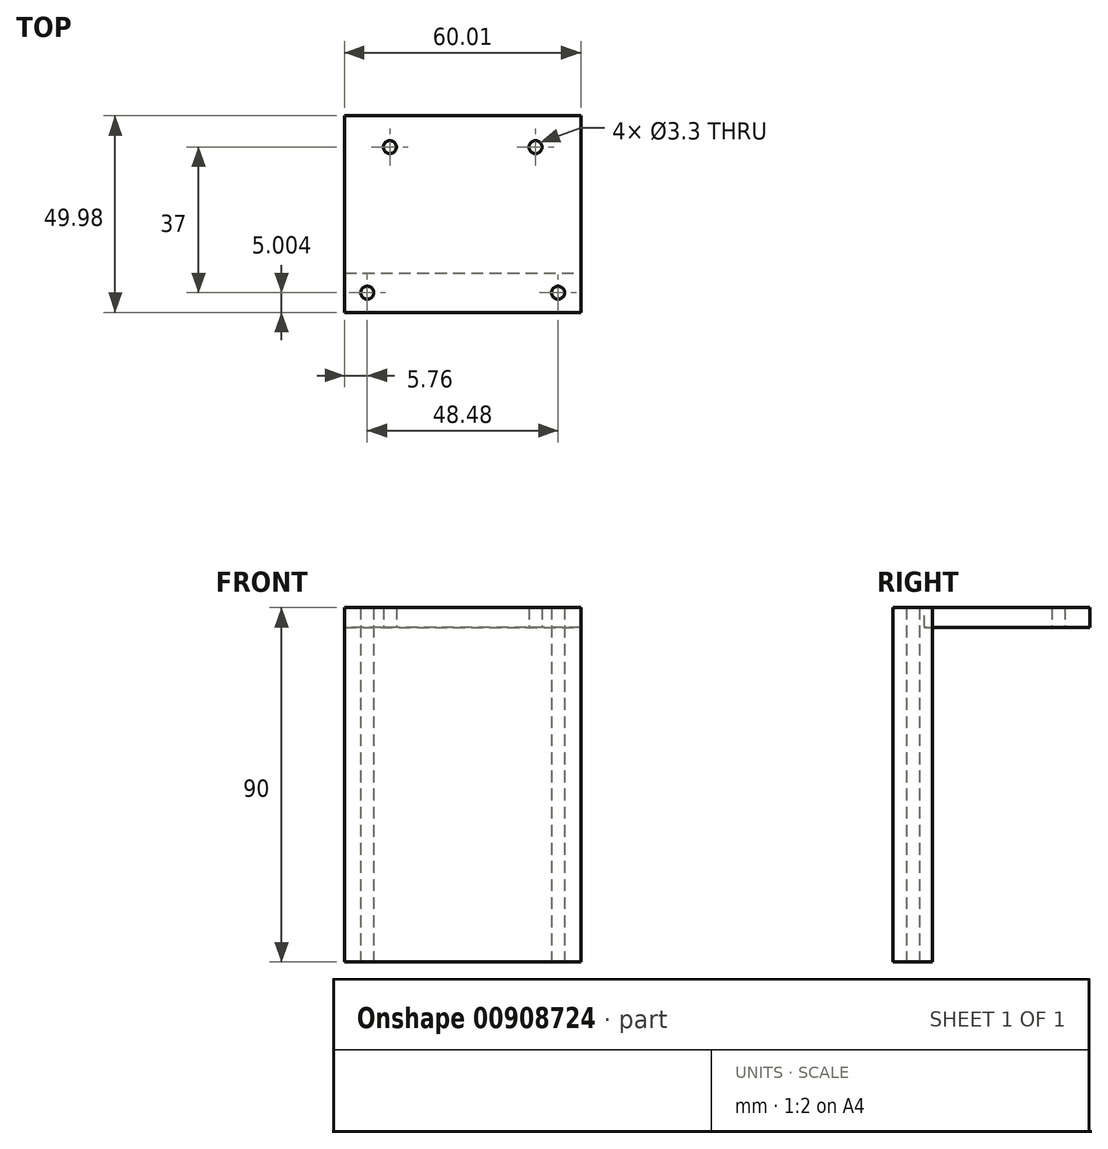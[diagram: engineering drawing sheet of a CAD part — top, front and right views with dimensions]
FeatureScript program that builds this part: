
annotation { "Feature Type Name" : "Feature", "Feature Type Description" : "" }
export const myFeature = defineFeature(function(context is Context, id is Id, definition is map)
    precondition{}
    {
        {
            var Q0;
            Q0=qCreatedBy(makeId("Top.planeOp"),FACE);
            var sketch = newSketch(context, id + "F0", { "sketchPlane" : qUnion([Q0])});
            skLineSegment(sketch, "E0.top", {"start": v(10.01, -7.98) * mm, "end": v(-49.99, -7.98) * mm});
            skLineSegment(sketch, "E1", {"start": v(-20, 34.02) * mm, "end": v(-38.5, 34.02) * mm, "construction": true});
            skLineSegment(sketch, "E2", {"start": v(-20, 34.02) * mm, "end": v(-1.5, 34.02) * mm, "construction": true});
            skCircle(sketch, "E3", {"center": v(-38.5, 34.02) * mm, "radius": 1.65 * mm});
            skCircle(sketch, "E4", {"center": v(-1.5, 34.02) * mm, "radius": 1.65 * mm});
            skCircle(sketch, "E5", {"center": v(4.24, -2.98) * mm, "radius": 1.65 * mm});
            skCircle(sketch, "E6", {"center": v(-44.24, -2.98) * mm, "radius": 1.65 * mm});
            skLineSegment(sketch, "E7", {"start": v(-20, 34.02) * mm, "end": v(-20, -7.98) * mm, "construction": true});
            skPoint(sketch, "E7.endSnap0", {"position": v(-20, 2.02) * mm});
            skLineSegment(sketch, "E8", {"start": v(-20, -7.98) * mm, "end": v(-20, 34.02) * mm, "construction": true});
            skLineSegment(sketch, "E9", {"start": v(10.01, -7.98) * mm, "end": v(10.01, 2.02) * mm});
            skLineSegment(sketch, "E10", {"start": v(-49.99, -7.98) * mm, "end": v(-49.99, 2.02) * mm});
            skLineSegment(sketch, "E11", {"start": v(-49.99, 2.02) * mm, "end": v(10.01, 2.02) * mm});
            skLineSegment(sketch, "E12.top", {"start": v(10.01, 2.02) * mm, "end": v(-49.99, 2.02) * mm});
            skSolve(sketch);
        }
        {
            var Q0;
            Q0=qCreatedBy(makeId("Front.planeOp"),FACE);
            var sketch = newSketch(context, id + "F1", { "sketchPlane" : qUnion([Q0])});
            skLineSegment(sketch, "E13", {"start": v(0, 0) * mm, "end": v(0, 68.75) * mm, "construction": true});
            skLineSegment(sketch, "E14.bottom", {"start": v(10, 85) * mm, "end": v(-50, 85) * mm});
            skLineSegment(sketch, "E14.top", {"start": v(10, 90) * mm, "end": v(-50, 90) * mm});
            skLineSegment(sketch, "E14.left", {"start": v(10, 85) * mm, "end": v(10, 90) * mm});
            skLineSegment(sketch, "E14.right", {"start": v(-50, 85) * mm, "end": v(-50, 90) * mm});
            skSolve(sketch);
        }
        {
            var Q0;
            {var subQ1=sQuery(id+"F0.wireOp",EDGE,"E0.top");Q0=makeQuery(id+"F0.imprint","IMPRINT",FACE,{"disambiguationData":[TD([[makeQuery(id+"F0.imprint","IMPRINT",EDGE,{"derivedFrom":subQ1}),-1.0]])]});}
            extrude(context, id + "F2", {"entities" : qUnion([Q0]), "depth" : 90 * mm, "offsetDistance" : 25 * mm});
        }
        {
            var Q0;
            Q0=qSketchRegion(id+"F1",true);
            extrude(context, id + "F3", {"entities" : qUnion([Q0]), "operationType" : NewBodyOperationType.ADD, "oppositeDirection" : true, "depth" : 42 * mm, "offsetDistance" : 25 * mm});
        }
        {
            var Q0;
            Q0=makeQuery(id+"F0.imprint","IMPRINT",FACE,{"disambiguationData":[TD([[makeQuery(id+"F0.imprint","IMPRINT",EDGE,{"derivedFrom":sQuery(id+"F0.wireOp",EDGE,"E5")}),1.0]])]});
            var Q1;
            Q1=makeQuery(id+"F0.imprint","IMPRINT",FACE,{"disambiguationData":[TD([[makeQuery(id+"F0.imprint","IMPRINT",EDGE,{"derivedFrom":sQuery(id+"F0.wireOp",EDGE,"E6")}),1.0]])]});
            var Q2;
            Q2=makeQuery(id+"F0.imprint","IMPRINT",FACE,{"disambiguationData":[TD([[makeQuery(id+"F0.imprint","IMPRINT",EDGE,{"derivedFrom":sQuery(id+"F0.wireOp",EDGE,"E3")}),1.0]])]});
            var Q3;
            Q3=makeQuery(id+"F0.imprint","IMPRINT",FACE,{"disambiguationData":[TD([[makeQuery(id+"F0.imprint","IMPRINT",EDGE,{"derivedFrom":sQuery(id+"F0.wireOp",EDGE,"E4")}),1.0]])]});
            extrude(context, id + "F4", {"entities" : qUnion([Q0, Q1, Q2, Q3]), "operationType" : NewBodyOperationType.REMOVE, "depth" : 97 * mm, "offsetDistance" : 25 * mm});
        }
    });
